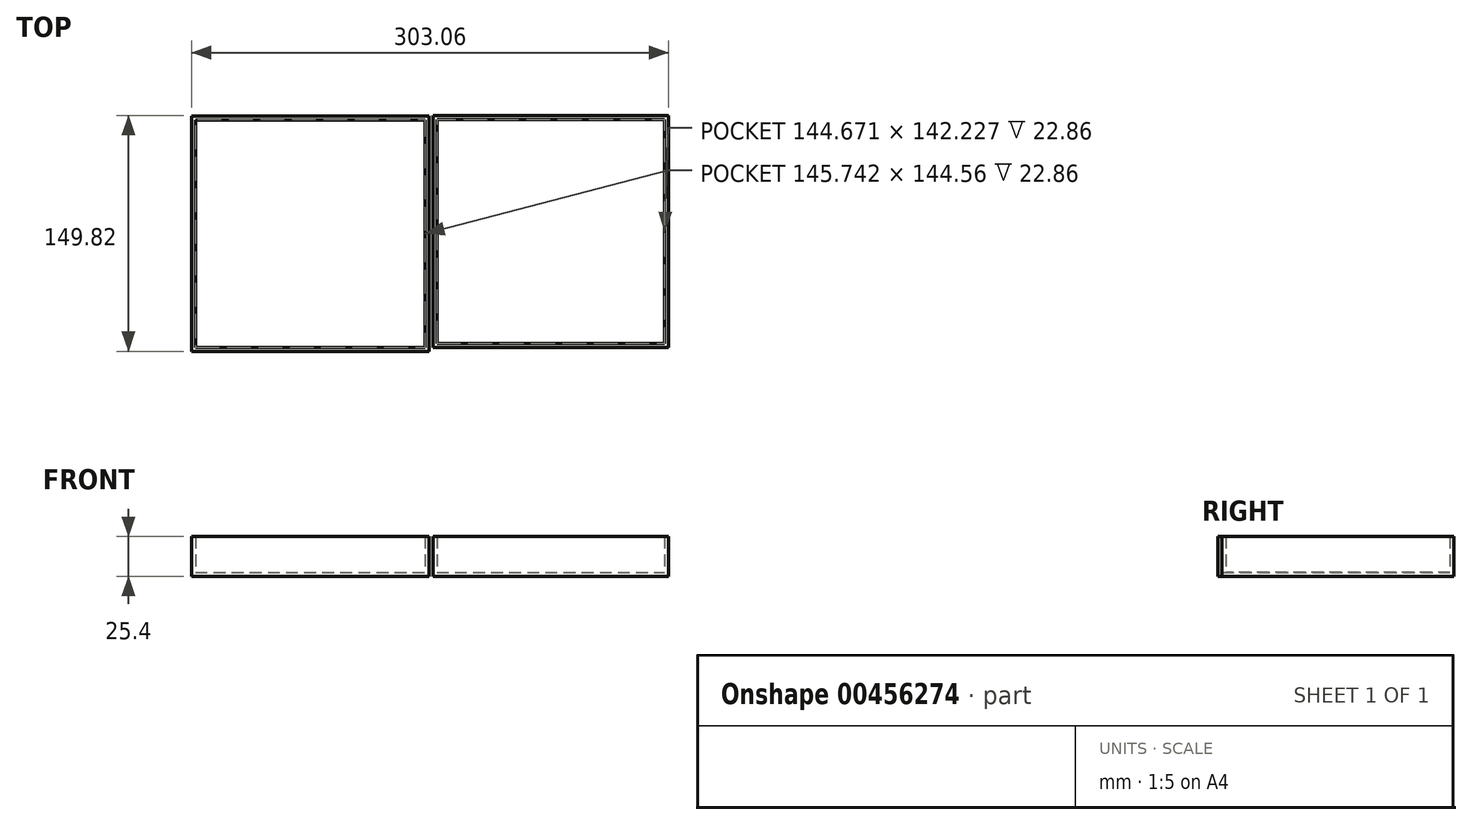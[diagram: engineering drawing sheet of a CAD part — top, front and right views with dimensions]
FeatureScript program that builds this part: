
annotation { "Feature Type Name" : "Feature", "Feature Type Description" : "" }
export const myFeature = defineFeature(function(context is Context, id is Id, definition is map)
    precondition{}
    {
        {
            var Q0;
            Q0=qCreatedBy(makeId("Top.planeOp"),FACE);
            var sketch = newSketch(context, id + "F0", { "sketchPlane" : qUnion([Q0])});
            skLineSegment(sketch, "E0.bottom", {"start": v(-73.82, -74.42) * mm, "end": v(77, -74.42) * mm});
            skLineSegment(sketch, "E0.top", {"start": v(-73.82, 75.22) * mm, "end": v(77, 75.22) * mm});
            skLineSegment(sketch, "E0.left", {"start": v(-73.82, -74.42) * mm, "end": v(-73.82, 75.22) * mm});
            skLineSegment(sketch, "E0.right", {"start": v(77, -74.42) * mm, "end": v(77, 75.22) * mm});
            skSolve(sketch);
        }
        {
            var Q0;
            Q0 = qSketchRegion(id + "F0", true);
            extrude(context, id + "F1", {"entities" : qUnion([Q0]), "depth" : 25.4 * mm});
        }
        {
            var Q0;
            Q0=makeQuery(id+"F1.opExtrude","CAP_FACE",FACE,{"disambiguationData":[OSD([sQuery(id+"F0.wireOp",EDGE,"E0.bottom"),sQuery(id+"F0.wireOp",EDGE,"E0.top"),sQuery(id+"F0.wireOp",EDGE,"E0.left"),sQuery(id+"F0.wireOp",EDGE,"E0.right")])],"isStart":false});
            shell(context, id + "F2", {"entities" : qUnion([Q0]), "thickness" : 2.54 * mm});
        }
        {
            var Q0;
            Q0=qCreatedBy(makeId("Top.planeOp"),FACE);
            var sketch = newSketch(context, id + "F3", { "sketchPlane" : qUnion([Q0])});
            skLineSegment(sketch, "E1.bottom", {"start": v(79.5, 75.4) * mm, "end": v(229.24, 75.4) * mm});
            skLineSegment(sketch, "E1.top", {"start": v(79.5, -71.9) * mm, "end": v(229.24, -71.9) * mm});
            skLineSegment(sketch, "E1.left", {"start": v(79.5, 75.4) * mm, "end": v(79.5, -71.9) * mm});
            skLineSegment(sketch, "E1.right", {"start": v(229.24, 75.4) * mm, "end": v(229.24, -71.9) * mm});
            skSolve(sketch);
        }
        {
            var Q0;
            Q0 = qSketchRegion(id + "F3", true);
            extrude(context, id + "F4", {"entities" : qUnion([Q0]), "depth" : 25.4 * mm});
        }
        {
            var Q0;
            Q0=makeQuery(id+"F4.opExtrude","CAP_FACE",FACE,{"disambiguationData":[OSD([sQuery(id+"F3.wireOp",EDGE,"E1.bottom"),sQuery(id+"F3.wireOp",EDGE,"E1.top"),sQuery(id+"F3.wireOp",EDGE,"E1.left"),sQuery(id+"F3.wireOp",EDGE,"E1.right")])],"isStart":false});
            shell(context, id + "F5", {"entities" : qUnion([Q0]), "thickness" : 2.54 * mm});
        }
    });
